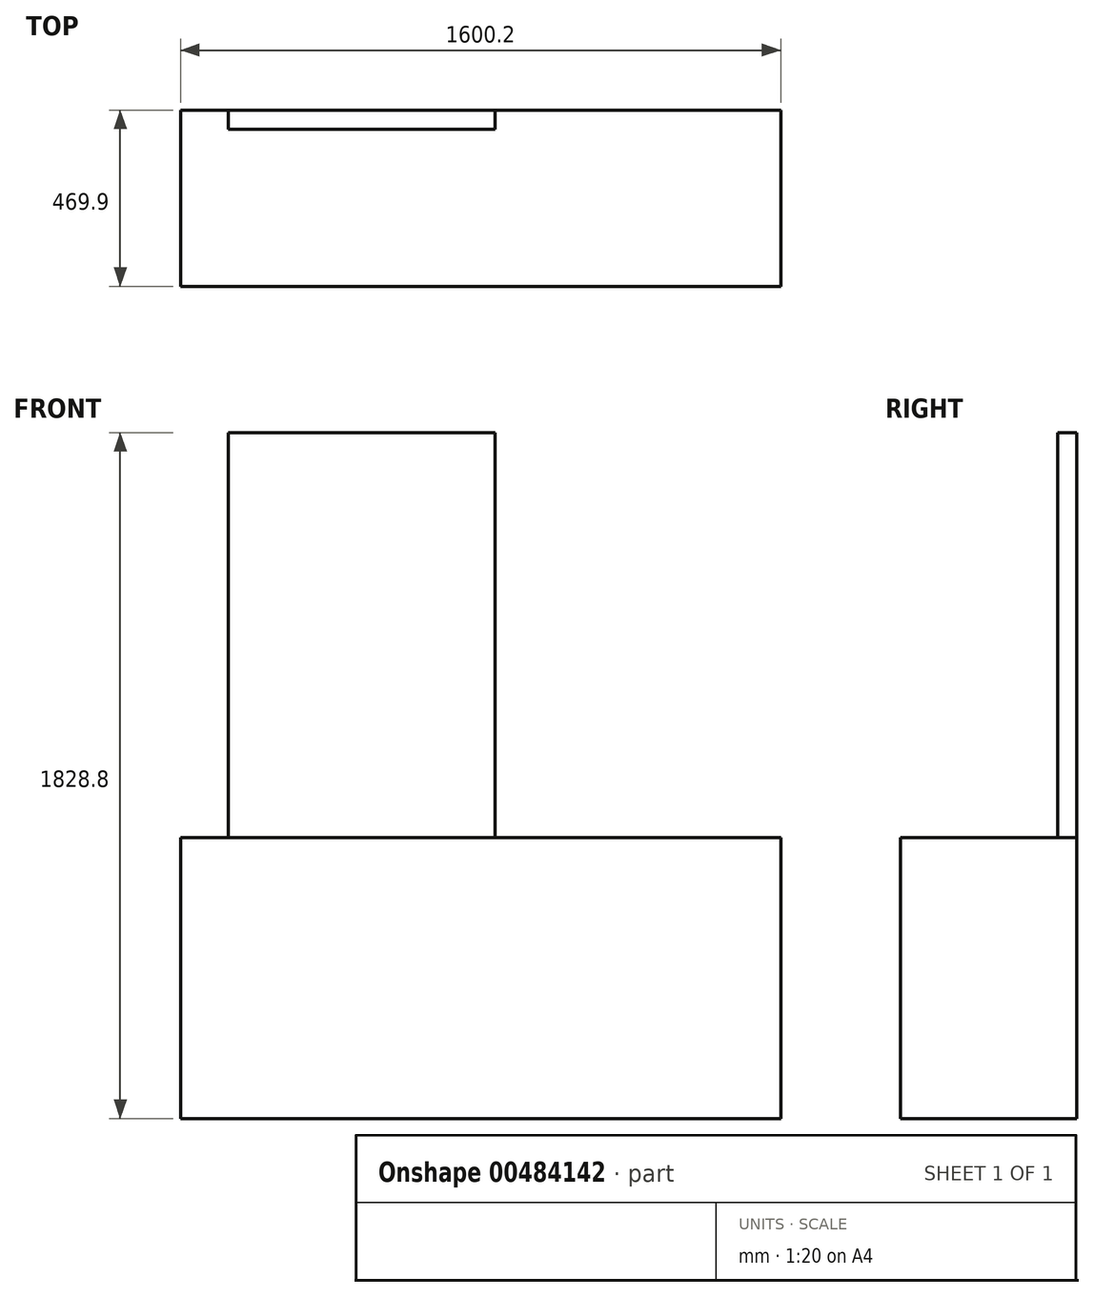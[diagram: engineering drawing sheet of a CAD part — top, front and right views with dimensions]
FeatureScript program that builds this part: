
annotation { "Feature Type Name" : "Feature", "Feature Type Description" : "" }
export const myFeature = defineFeature(function(context is Context, id is Id, definition is map)
    precondition{}
    {
        {
            var Q0;
            Q0=qCreatedBy(makeId("Front.planeOp"),FACE);
            var sketch = newSketch(context, id + "F0", { "sketchPlane" : qUnion([Q0])});
            skLineSegment(sketch, "E0.bottom", {"start": v(0, 0) * mm, "end": v(1600.2, 0) * mm});
            skLineSegment(sketch, "E0.top", {"start": v(0, 749.3) * mm, "end": v(1600.2, 749.3) * mm});
            skLineSegment(sketch, "E0.left", {"start": v(0, 0) * mm, "end": v(0, 749.3) * mm});
            skLineSegment(sketch, "E0.right", {"start": v(1600.2, 0) * mm, "end": v(1600.2, 749.3) * mm});
            skSolve(sketch);
        }
        {
            var Q0;
            Q0 = qSketchRegion(id + "F0", true);
            extrude(context, id + "F1", {"entities" : qUnion([Q0]), "depth" : 469.9 * mm, "offsetDistance" : 25.4 * mm});
        }
        {
            var Q0;
            Q0=makeQuery(id+"F1.opExtrude","CAP_FACE",FACE,{"disambiguationData":[OSD([sQuery(id+"F0.wireOp",EDGE,"E0.bottom"),sQuery(id+"F0.wireOp",EDGE,"E0.top"),sQuery(id+"F0.wireOp",EDGE,"E0.left"),sQuery(id+"F0.wireOp",EDGE,"E0.right")])],"isStart":true});
            var sketch = newSketch(context, id + "F2", { "sketchPlane" : qUnion([Q0])});
            skLineSegment(sketch, "E1.bottom", {"start": v(-127, 749.3) * mm, "end": v(-838.2, 749.3) * mm});
            skLineSegment(sketch, "E1.top", {"start": v(-127, 1828.8) * mm, "end": v(-838.2, 1828.8) * mm});
            skLineSegment(sketch, "E1.left", {"start": v(-127, 749.3) * mm, "end": v(-127, 1828.8) * mm});
            skLineSegment(sketch, "E1.right", {"start": v(-838.2, 749.3) * mm, "end": v(-838.2, 1828.8) * mm});
            skSolve(sketch);
        }
        {
            var Q0;
            Q0 = qSketchRegion(id + "F2", true);
            extrude(context, id + "F3", {"entities" : qUnion([Q0]), "operationType" : NewBodyOperationType.ADD, "oppositeDirection" : true, "depth" : 50.8 * mm, "offsetDistance" : 25.4 * mm});
        }
    });
